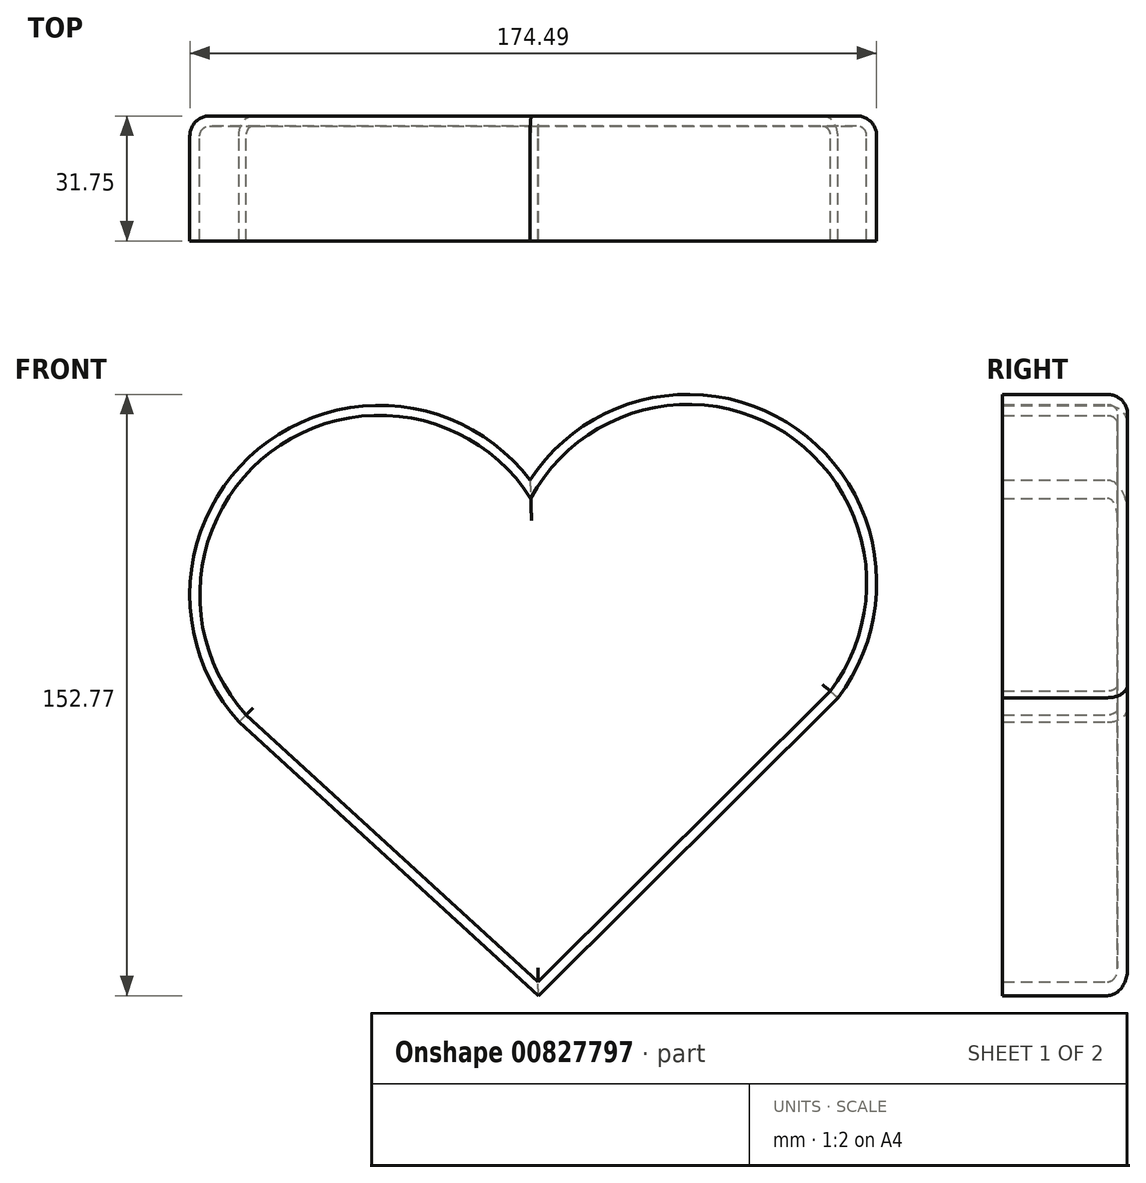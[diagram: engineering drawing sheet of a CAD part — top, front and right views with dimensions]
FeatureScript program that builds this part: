
annotation { "Feature Type Name" : "Feature", "Feature Type Description" : "" }
export const myFeature = defineFeature(function(context is Context, id is Id, definition is map)
    precondition{}
    {
        {
            var Q0;
            Q0=qCreatedBy(makeId("Front.planeOp"),FACE);
            var sketch = newSketch(context, id + "F0", { "sketchPlane" : qUnion([Q0])});
            skLineSegment(sketch, "E0", {"start": v(-76.08, -6.18) * mm, "end": v(0, -75.7) * mm});
            skArc(sketch, "E1", {"start": v(-2.12, 55.32) * mm, "mid": v(-71.2, 63.17) * mm, "end": v(-76.08, -6.18) * mm});
            skArc(sketch, "E2", {"start": v(76.05, 0) * mm, "mid": v(65.7, 68.27) * mm, "end": v(-2.12, 55.32) * mm});
            skLineSegment(sketch, "E3", {"start": v(0, -75.7) * mm, "end": v(76.05, 0) * mm});
            skPoint(sketch, "E4.orphan", {"position": v(0, 0) * mm});
            skSolve(sketch);
        }
        {
            var Q0;
            Q0=makeQuery(id+"F0.imprint","IMPRINT",FACE,{"disambiguationData":[TD([[makeQuery(id+"F0.imprint","IMPRINT",EDGE,{"derivedFrom":sQuery(id+"F0.wireOp",EDGE,"E0")}),1.0]])]});
            extrude(context, id + "F1", {"entities" : qUnion([Q0]), "depth" : 31.75 * mm, "offsetDistance" : 25.4 * mm});
        }
        {
            var Q0;
            Q0=makeQuery(id+"F1.opExtrude","CAP_FACE",FACE,{"disambiguationData":[OSD([sQuery(id+"F0.wireOp",EDGE,"E0"),sQuery(id+"F0.wireOp",EDGE,"E1"),sQuery(id+"F0.wireOp",EDGE,"E2"),sQuery(id+"F0.wireOp",EDGE,"E3")])],"isStart":true});
            fillet(context, id + "F2", {"entities" : qUnion([Q0]), "radius" : 5.08 * mm, "tangentPropagation" : true, "allowEdgeOverflow" : false});
        }
        {
            var Q0;
            Q0=makeQuery(id+"F1.opExtrude","CAP_FACE",FACE,{"disambiguationData":[OSD([sQuery(id+"F0.wireOp",EDGE,"E0"),sQuery(id+"F0.wireOp",EDGE,"E1"),sQuery(id+"F0.wireOp",EDGE,"E2"),sQuery(id+"F0.wireOp",EDGE,"E3")])],"isStart":false});
            shell(context, id + "F3", {"entities" : qUnion([Q0]), "thickness" : 2.54 * mm});
        }
    });
